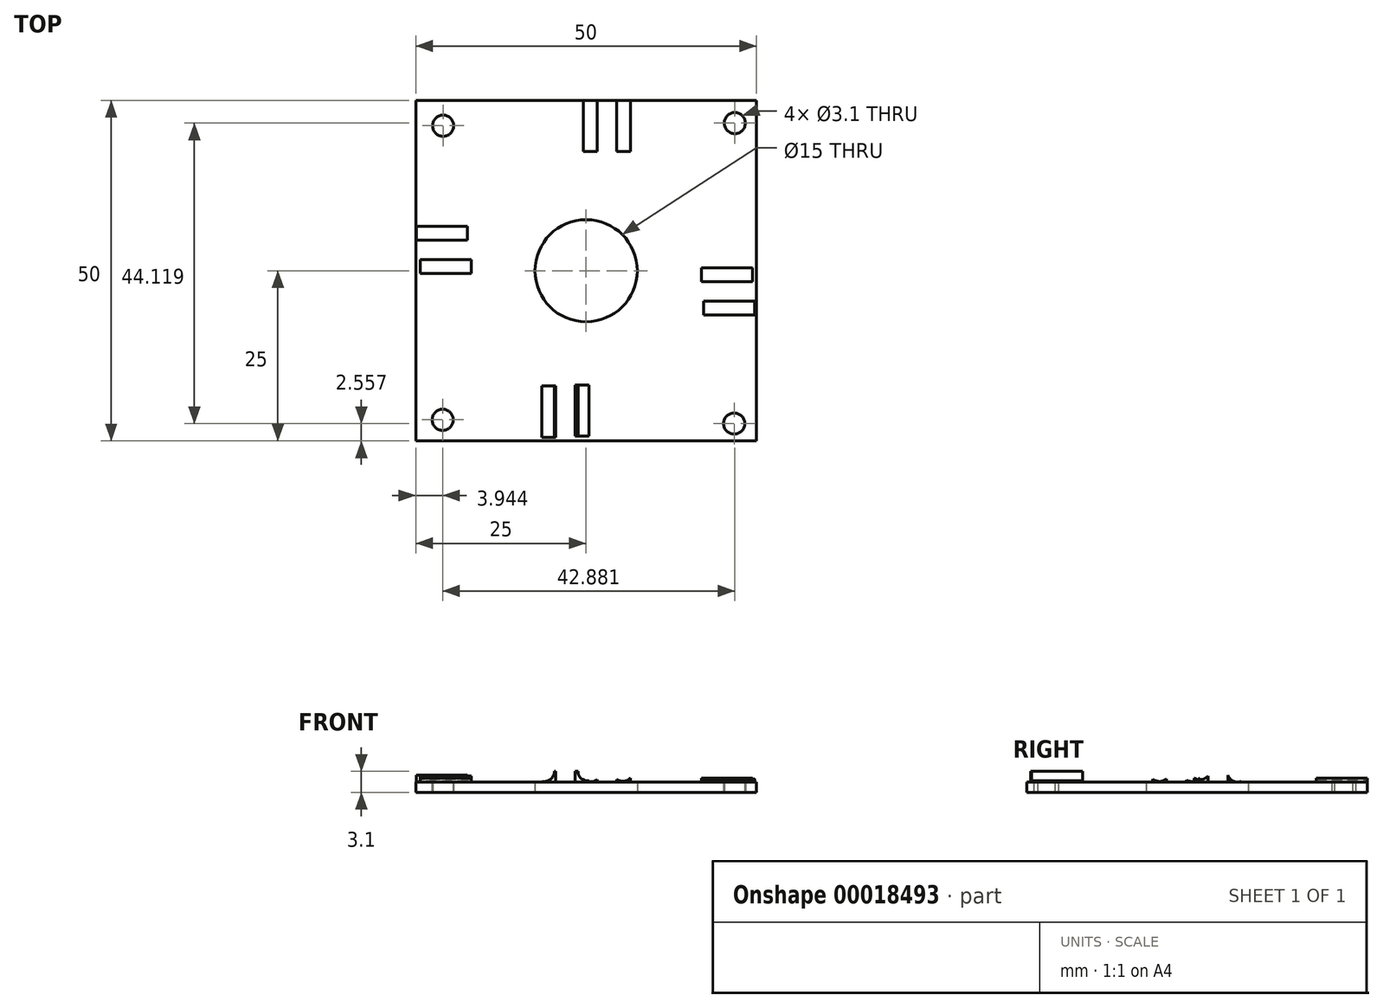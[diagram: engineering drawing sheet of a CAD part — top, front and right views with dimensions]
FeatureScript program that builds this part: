
annotation { "Feature Type Name" : "Feature", "Feature Type Description" : "" }
export const myFeature = defineFeature(function(context is Context, id is Id, definition is map)
    precondition{}
    {
        {
            var Q0;
            Q0=qCreatedBy(makeId("Top.planeOp"),FACE);
            var sketch = newSketch(context, id + "F0", { "sketchPlane" : qUnion([Q0])});
            skLineSegment(sketch, "E0.rect.bottom", {"start": v(25, -25) * mm, "end": v(-25, -25) * mm});
            skLineSegment(sketch, "E0.rect.top", {"start": v(25, 25) * mm, "end": v(-25, 25) * mm});
            skLineSegment(sketch, "E0.rect.left", {"start": v(25, -25) * mm, "end": v(25, 25) * mm});
            skLineSegment(sketch, "E0.rect.right", {"start": v(-25, -25) * mm, "end": v(-25, 25) * mm});
            skPoint(sketch, "E0.rect.middle", {"position": v(0, 0) * mm});
            skCircle(sketch, "E1", {"center": v(0, 0) * mm, "radius": 7.5 * mm});
            skLineSegment(sketch, "E2", {"start": v(0, 7.5) * mm, "end": v(10.23, 7.5) * mm, "construction": true});
            skLineSegment(sketch, "E3", {"start": v(0, -7.5) * mm, "end": v(10.24, -7.5) * mm, "construction": true});
            skCircle(sketch, "E4", {"center": v(-20.99, 21.3) * mm, "radius": 1.55 * mm});
            skCircle(sketch, "E5", {"center": v(21.82, 21.68) * mm, "radius": 1.55 * mm});
            skCircle(sketch, "E6", {"center": v(-21.06, -21.9) * mm, "radius": 1.55 * mm});
            skCircle(sketch, "E7", {"center": v(21.73, -22.44) * mm, "radius": 1.55 * mm});
            skSolve(sketch);
        }
        {
            var Q0;
            Q0=makeQuery(id+"F0.imprint","IMPRINT",FACE,{"disambiguationData":[TD([[makeQuery(id+"F0.imprint","IMPRINT",EDGE,{"derivedFrom":sQuery(id+"F0.wireOp",EDGE,"E0.rect.bottom")}),-1.0]])]});
            extrude(context, id + "F1", {"entities" : qUnion([Q0]), "depth" : 1.5 * mm});
        }
        {
            var Q0;
            Q0=makeQuery(id+"F1.opExtrude","CAP_FACE",FACE,{"disambiguationData":[OSD([sQuery(id+"F0.wireOp",EDGE,"E0.rect.bottom"),sQuery(id+"F0.wireOp",EDGE,"E0.rect.top"),sQuery(id+"F0.wireOp",EDGE,"E0.rect.left"),sQuery(id+"F0.wireOp",EDGE,"E0.rect.right"),sQuery(id+"F0.wireOp",EDGE,"E1"),sQuery(id+"F0.wireOp",EDGE,"E4"),sQuery(id+"F0.wireOp",EDGE,"E5"),sQuery(id+"F0.wireOp",EDGE,"E6"),sQuery(id+"F0.wireOp",EDGE,"E7")])],"isStart":false});
            var sketch = newSketch(context, id + "F2", { "sketchPlane" : qUnion([Q0])});
            skLineSegment(sketch, "E8.bottom", {"start": v(-0.4, 25) * mm, "end": v(1.6, 25) * mm});
            skLineSegment(sketch, "E8.top", {"start": v(-0.4, 17.5) * mm, "end": v(1.6, 17.5) * mm});
            skLineSegment(sketch, "E8.left", {"start": v(-0.4, 25) * mm, "end": v(-0.4, 17.5) * mm});
            skLineSegment(sketch, "E8.right", {"start": v(1.6, 25) * mm, "end": v(1.6, 17.5) * mm});
            skSolve(sketch);
        }
        {
            var Q0;
            Q0=makeQuery(id+"F2.imprint","IMPRINT",FACE,{"disambiguationData":[TD([[makeQuery(id+"F2.imprint","IMPRINT",EDGE,{"derivedFrom":sQuery(id+"F2.wireOp",EDGE,"E8.bottom")}),1.0]])]});
            extrude(context, id + "F3", {"entities" : qUnion([Q0]), "operationType" : NewBodyOperationType.ADD, "depth" : 1.6 * mm});
        }
        {
            var Q0;
            Q0=makeQuery(id+"F3.boolean.opBoolean","MERGE",FACE,{"derivedFrom":[makeQuery(id+"F1.opExtrude","SWEPT_FACE",FACE,{"disambiguationData":[OSD([sQuery(id+"F0.wireOp",EDGE,"E0.rect.top")])]}),makeQuery(id+"F3.opExtrude","SWEPT_FACE",FACE,{"disambiguationData":[OSD([sQuery(id+"F2.wireOp",EDGE,"E8.bottom")])]})]});
            var sketch = newSketch(context, id + "F4", { "sketchPlane" : qUnion([Q0])});
            skCircle(sketch, "E9", {"center": v(-0.6, 3.1) * mm, "radius": 1.55 * mm});
            skSolve(sketch);
        }
        {
            var Q0;
            {var subQ0=makeQuery(id+"F3.opExtrude","CAP_EDGE",EDGE,{"disambiguationData":[OSD([sQuery(id+"F2.wireOp",EDGE,"E8.bottom")])],"isStart":false});var subQ1=sQuery(id+"F4.wireOp",EDGE,"E9");var subQ3=makeQuery(id+"F4.imprint","INTERSECT",VERTEX,{"disambiguationData":[OD(0.0)],"derivedFrom":[subQ0,subQ1]});Q0=makeQuery(id+"F4.imprint","IMPRINT",FACE,{"disambiguationData":[TD([[makeQuery(id+"F4.imprint","IMPRINT",EDGE,{"disambiguationData":[TD([[subQ3,-1.0]])],"derivedFrom":subQ1}),1.0]])]});}
            extrude(context, id + "F5", {"entities" : qUnion([Q0]), "operationType" : NewBodyOperationType.REMOVE, "oppositeDirection" : true, "depth" : 25 * mm});
        }
        {
            var Q0;
            Q0=makeQuery(id+"F2.imprint","IMPRINT",FACE,{"disambiguationData":[TD([[makeQuery(id+"F2.imprint","IMPRINT",EDGE,{"derivedFrom":sQuery(id+"F2.wireOp",EDGE,"E8.top")}),-1.0]])]});
            var sketch = newSketch(context, id + "F6", { "sketchPlane" : qUnion([Q0])});
            skLineSegment(sketch, "E10.bottom", {"start": v(4.5, 24.98) * mm, "end": v(6.5, 24.98) * mm});
            skLineSegment(sketch, "E10.top", {"start": v(4.5, 17.48) * mm, "end": v(6.5, 17.48) * mm});
            skLineSegment(sketch, "E10.left", {"start": v(4.5, 24.98) * mm, "end": v(4.5, 17.48) * mm});
            skLineSegment(sketch, "E10.right", {"start": v(6.5, 24.98) * mm, "end": v(6.5, 17.48) * mm});
            skSolve(sketch);
        }
        {
            var Q0;
            Q0=makeQuery(id+"F6.imprint","IMPRINT",FACE,{"disambiguationData":[TD([[makeQuery(id+"F6.imprint","IMPRINT",EDGE,{"derivedFrom":sQuery(id+"F6.wireOp",EDGE,"E10.bottom")}),-1.0]])]});
            extrude(context, id + "F7", {"entities" : qUnion([Q0]), "operationType" : NewBodyOperationType.ADD, "depth" : 1.6 * mm});
        }
        {
            var Q0;
            Q0=makeQuery(id+"F3.boolean.opBoolean","MERGE",FACE,{"derivedFrom":[makeQuery(id+"F1.opExtrude","SWEPT_FACE",FACE,{"disambiguationData":[OSD([sQuery(id+"F0.wireOp",EDGE,"E0.rect.top")])]}),makeQuery(id+"F3.opExtrude","SWEPT_FACE",FACE,{"disambiguationData":[OSD([sQuery(id+"F2.wireOp",EDGE,"E8.bottom")])]})]});
            var sketch = newSketch(context, id + "F8", { "sketchPlane" : qUnion([Q0])});
            skCircle(sketch, "E11", {"center": v(-5.4, 3.18) * mm, "radius": 1.55 * mm});
            skSolve(sketch);
        }
        {
            var Q0;
            Q0=makeQuery(id+"F8.imprint","IMPRINT",FACE,{"disambiguationData":[TD([[makeQuery(id+"F8.imprint","IMPRINT",EDGE,{"derivedFrom":sQuery(id+"F8.wireOp",EDGE,"E11")}),1.0]])]});
            extrude(context, id + "F9", {"entities" : qUnion([Q0]), "operationType" : NewBodyOperationType.REMOVE, "oppositeDirection" : true, "depth" : 25 * mm});
        }
        {
            var Q0;
            Q0=makeQuery(id+"F2.imprint","IMPRINT",FACE,{"disambiguationData":[TD([[makeQuery(id+"F2.imprint","IMPRINT",EDGE,{"derivedFrom":sQuery(id+"F2.wireOp",EDGE,"E8.top")}),-1.0]])]});
            var sketch = newSketch(context, id + "F10", { "sketchPlane" : qUnion([Q0])});
            skLineSegment(sketch, "E12.bottom", {"start": v(-24.34, 1.6) * mm, "end": v(-16.84, 1.6) * mm});
            skLineSegment(sketch, "E12.top", {"start": v(-24.34, -0.4) * mm, "end": v(-16.84, -0.4) * mm});
            skLineSegment(sketch, "E12.left", {"start": v(-24.34, 1.6) * mm, "end": v(-24.34, -0.4) * mm});
            skLineSegment(sketch, "E12.right", {"start": v(-16.84, 1.6) * mm, "end": v(-16.84, -0.4) * mm});
            skLineSegment(sketch, "E13.bottom", {"start": v(-24.9, 4.5) * mm, "end": v(-17.4, 4.5) * mm});
            skLineSegment(sketch, "E13.top", {"start": v(-24.9, 6.5) * mm, "end": v(-17.4, 6.5) * mm});
            skLineSegment(sketch, "E13.left", {"start": v(-24.9, 4.5) * mm, "end": v(-24.9, 6.5) * mm});
            skLineSegment(sketch, "E13.right", {"start": v(-17.4, 4.5) * mm, "end": v(-17.4, 6.5) * mm});
            skSolve(sketch);
        }
        {
            var Q0;
            Q0 = qSketchRegion(id + "F10", true);
            extrude(context, id + "F11", {"entities" : qUnion([Q0]), "operationType" : NewBodyOperationType.ADD, "depth" : 1.6 * mm});
        }
        {
            var Q0;
            Q0=makeQuery(id+"F1.opExtrude","SWEPT_FACE",FACE,{"disambiguationData":[OSD([sQuery(id+"F0.wireOp",EDGE,"E0.rect.right")])]});
            var sketch = newSketch(context, id + "F12", { "sketchPlane" : qUnion([Q0])});
            skCircle(sketch, "E14", {"center": v(-0.42, 3.42) * mm, "radius": 1.55 * mm});
            skCircle(sketch, "E15", {"center": v(-5.95, 3.07) * mm, "radius": 1.55 * mm});
            skSolve(sketch);
        }
        {
            var Q0;
            Q0 = qSketchRegion(id + "F12", true);
            extrude(context, id + "F13", {"entities" : qUnion([Q0]), "operationType" : NewBodyOperationType.REMOVE, "oppositeDirection" : true, "depth" : 25 * mm});
        }
        {
            var Q0;
            Q0=makeQuery(id+"F2.imprint","IMPRINT",FACE,{"disambiguationData":[TD([[makeQuery(id+"F2.imprint","IMPRINT",EDGE,{"derivedFrom":sQuery(id+"F2.wireOp",EDGE,"E8.top")}),-1.0]])]});
            var sketch = newSketch(context, id + "F14", { "sketchPlane" : qUnion([Q0])});
            skLineSegment(sketch, "E16.bottom", {"start": v(-1.6, -24.3) * mm, "end": v(0.4, -24.3) * mm});
            skLineSegment(sketch, "E16.top", {"start": v(-1.6, -16.8) * mm, "end": v(0.4, -16.8) * mm});
            skLineSegment(sketch, "E16.left", {"start": v(-1.6, -24.3) * mm, "end": v(-1.6, -16.8) * mm});
            skLineSegment(sketch, "E16.right", {"start": v(0.4, -24.3) * mm, "end": v(0.4, -16.8) * mm});
            skLineSegment(sketch, "E17.bottom", {"start": v(-6.5, -24.45) * mm, "end": v(-4.5, -24.45) * mm});
            skLineSegment(sketch, "E17.top", {"start": v(-6.5, -16.95) * mm, "end": v(-4.5, -16.95) * mm});
            skLineSegment(sketch, "E17.left", {"start": v(-6.5, -24.45) * mm, "end": v(-6.5, -16.95) * mm});
            skLineSegment(sketch, "E17.right", {"start": v(-4.5, -24.45) * mm, "end": v(-4.5, -16.95) * mm});
            skSolve(sketch);
        }
        {
            var Q0;
            Q0 = qSketchRegion(id + "F14", true);
            var Q1;
            Q1 = qSketchRegion(id + "F20eHt2Xa6kNqZN_1", true);
            extrude(context, id + "F15", {"entities" : qUnion([Q0, Q1]), "operationType" : NewBodyOperationType.ADD, "depth" : 1.6 * mm});
        }
        {
            var Q0;
            Q0=makeQuery(id+"F1.opExtrude","SWEPT_FACE",FACE,{"disambiguationData":[OSD([sQuery(id+"F0.wireOp",EDGE,"E0.rect.bottom")])]});
            var sketch = newSketch(context, id + "F16", { "sketchPlane" : qUnion([Q0])});
            skCircle(sketch, "E18", {"center": v(-6.2, 3.14) * mm, "radius": 1.55 * mm});
            skCircle(sketch, "E19", {"center": v(0.13, 3.01) * mm, "radius": 1.3 * mm});
            skSolve(sketch);
        }
        {
            var Q0;
            Q0 = qSketchRegion(id + "F16", true);
            extrude(context, id + "F17", {"entities" : qUnion([Q0]), "operationType" : NewBodyOperationType.REMOVE, "oppositeDirection" : true, "depth" : 25 * mm});
        }
        {
            var Q0;
            Q0=makeQuery(id+"F2.imprint","IMPRINT",FACE,{"disambiguationData":[TD([[makeQuery(id+"F2.imprint","IMPRINT",EDGE,{"derivedFrom":sQuery(id+"F2.wireOp",EDGE,"E8.top")}),-1.0]])]});
            var sketch = newSketch(context, id + "F18", { "sketchPlane" : qUnion([Q0])});
            skLineSegment(sketch, "E20.bottom", {"start": v(24.72, -6.5) * mm, "end": v(17.22, -6.5) * mm});
            skLineSegment(sketch, "E20.top", {"start": v(24.72, -4.5) * mm, "end": v(17.22, -4.5) * mm});
            skLineSegment(sketch, "E20.left", {"start": v(24.72, -6.5) * mm, "end": v(24.72, -4.5) * mm});
            skLineSegment(sketch, "E20.right", {"start": v(17.22, -6.5) * mm, "end": v(17.22, -4.5) * mm});
            skLineSegment(sketch, "E21.bottom", {"start": v(24.44, -1.6) * mm, "end": v(16.94, -1.6) * mm});
            skLineSegment(sketch, "E21.top", {"start": v(24.44, 0.4) * mm, "end": v(16.94, 0.4) * mm});
            skLineSegment(sketch, "E21.left", {"start": v(24.44, -1.6) * mm, "end": v(24.44, 0.4) * mm});
            skLineSegment(sketch, "E21.right", {"start": v(16.94, -1.6) * mm, "end": v(16.94, 0.4) * mm});
            skSolve(sketch);
        }
        {
            var Q0;
            Q0 = qSketchRegion(id + "F18", true);
            extrude(context, id + "F19", {"entities" : qUnion([Q0]), "operationType" : NewBodyOperationType.ADD, "depth" : 1.6 * mm});
        }
        {
            var Q0;
            Q0=makeQuery(id+"F1.opExtrude","SWEPT_FACE",FACE,{"disambiguationData":[OSD([sQuery(id+"F0.wireOp",EDGE,"E0.rect.left")])]});
            var sketch = newSketch(context, id + "F20", { "sketchPlane" : qUnion([Q0])});
            skCircle(sketch, "E22", {"center": v(-5.52, 3.15) * mm, "radius": 1.55 * mm});
            skCircle(sketch, "E23", {"center": v(-0.76, 3.13) * mm, "radius": 1.55 * mm});
            skSolve(sketch);
        }
        {
            var Q0;
            Q0 = qSketchRegion(id + "F20", true);
            extrude(context, id + "F21", {"entities" : qUnion([Q0]), "operationType" : NewBodyOperationType.REMOVE, "oppositeDirection" : true, "depth" : 25 * mm});
        }
    });
